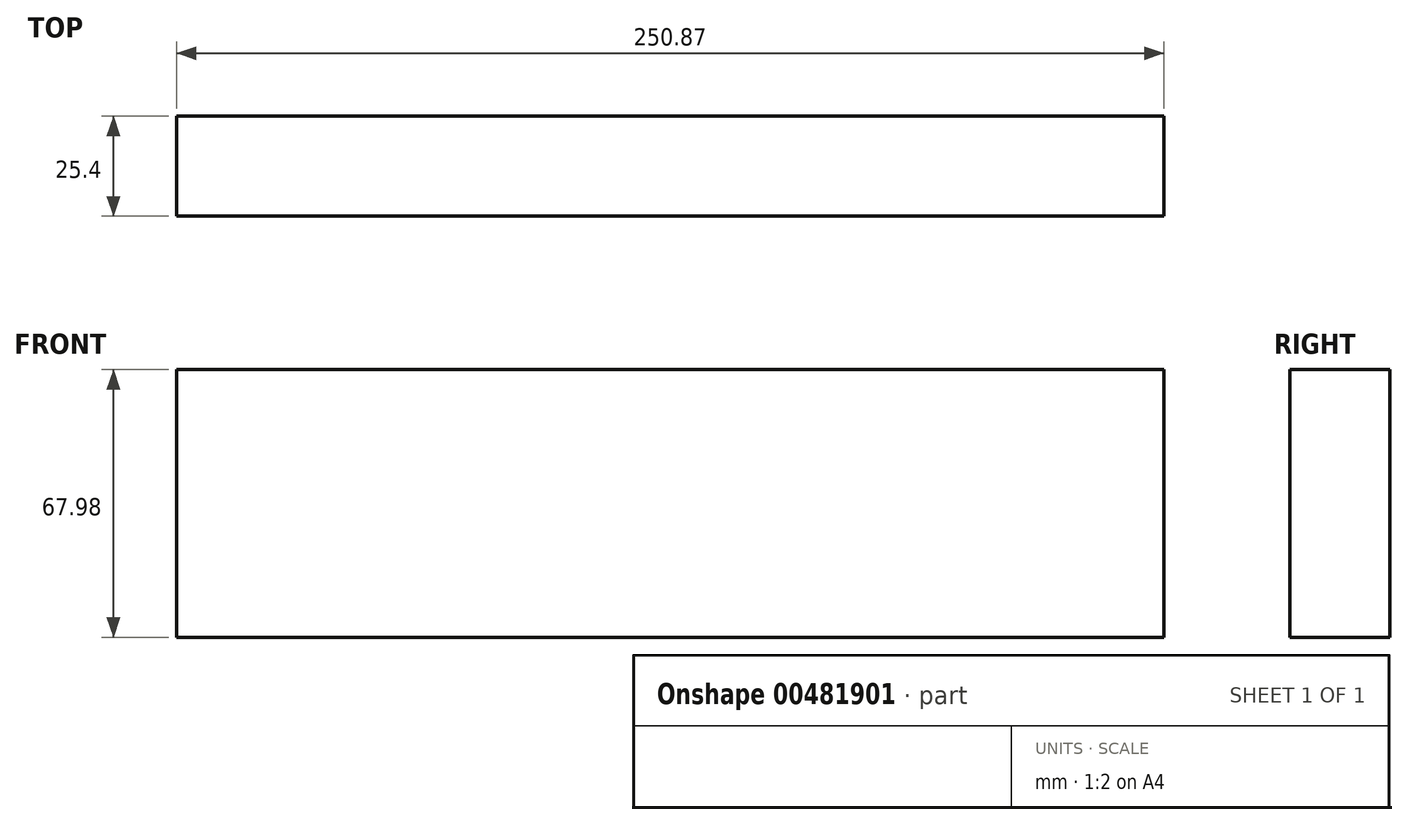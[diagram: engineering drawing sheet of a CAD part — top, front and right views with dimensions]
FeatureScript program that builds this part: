
annotation { "Feature Type Name" : "Feature", "Feature Type Description" : "" }
export const myFeature = defineFeature(function(context is Context, id is Id, definition is map)
    precondition{}
    {
        {
            var Q0;
            Q0=qCreatedBy(makeId("Front.planeOp"),FACE);
            var sketch = newSketch(context, id + "F0", { "sketchPlane" : qUnion([Q0])});
            skLineSegment(sketch, "E0.bottom", {"start": v(-122.1, 0) * mm, "end": v(128.76, 0) * mm});
            skLineSegment(sketch, "E0.top", {"start": v(-122.1, -67.98) * mm, "end": v(128.76, -67.98) * mm});
            skLineSegment(sketch, "E0.left", {"start": v(-122.1, 0) * mm, "end": v(-122.1, -67.98) * mm});
            skLineSegment(sketch, "E0.right", {"start": v(128.76, 0) * mm, "end": v(128.76, -67.98) * mm});
            skSolve(sketch);
        }
        {
            var Q0;
            Q0=makeQuery(id+"F0.imprint","IMPRINT",FACE,{"disambiguationData":[TD([[makeQuery(id+"F0.imprint","IMPRINT",EDGE,{"derivedFrom":sQuery(id+"F0.wireOp",EDGE,"E0.bottom")}),-1.0]])]});
            extrude(context, id + "F1", {"entities" : qUnion([Q0]), "oppositeDirection" : true, "depth" : 25.4 * mm});
        }
    });
